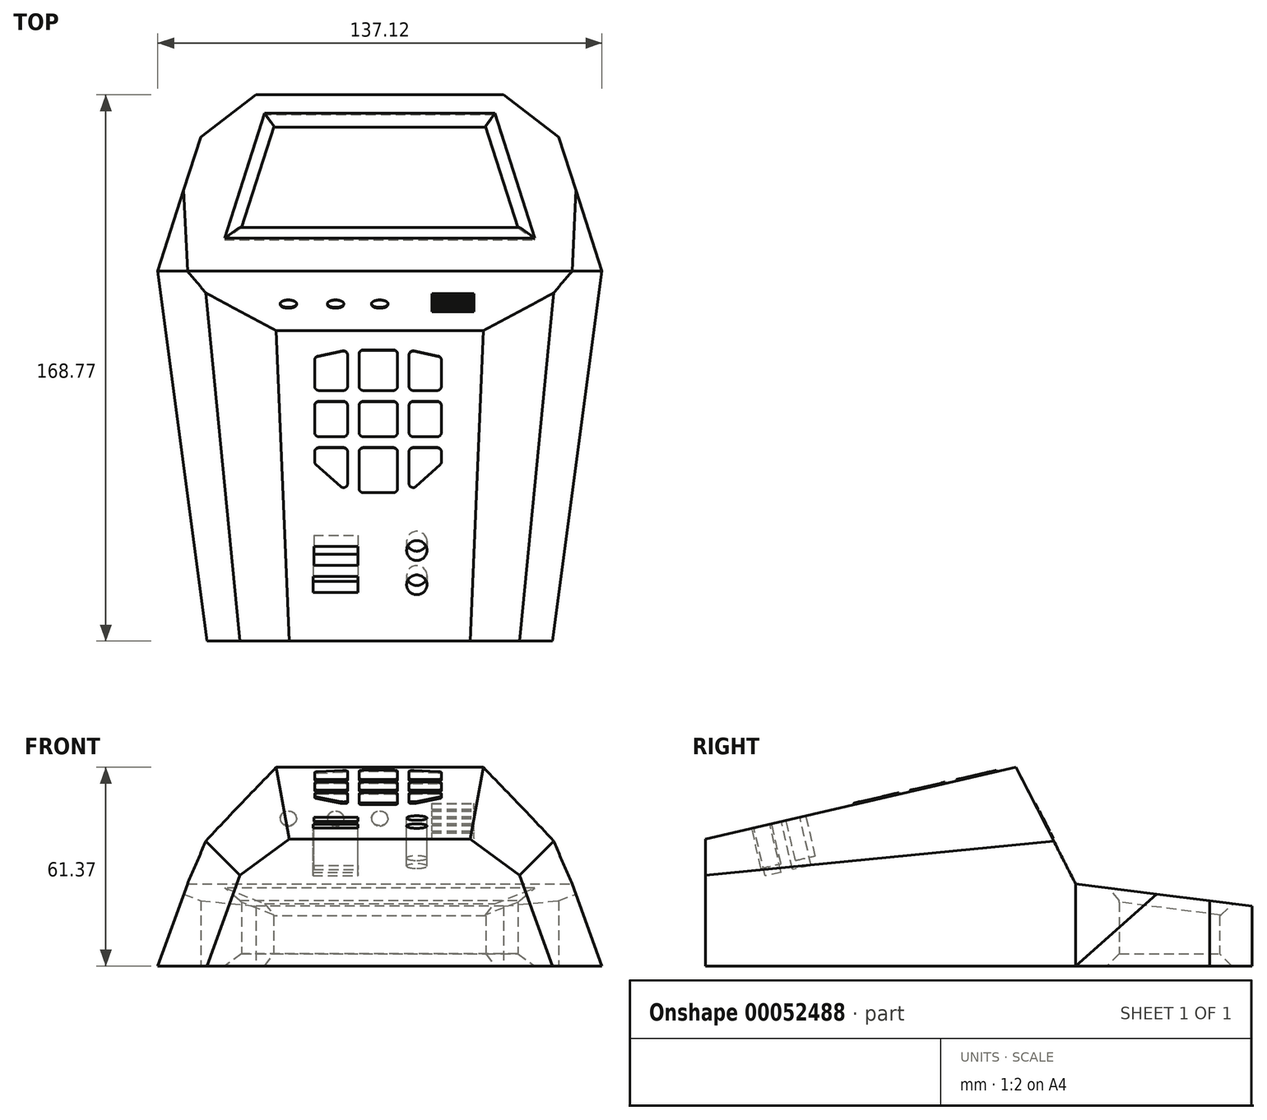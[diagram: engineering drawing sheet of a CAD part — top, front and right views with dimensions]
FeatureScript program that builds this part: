
annotation { "Feature Type Name" : "Feature", "Feature Type Description" : "" }
export const myFeature = defineFeature(function(context is Context, id is Id, definition is map)
    precondition{}
    {
        {
            var Q0;
            Q0=qCreatedBy(makeId("Front.planeOp"),FACE);
            var sketch = newSketch(context, id + "F0", { "sketchPlane" : qUnion([Q0])});
            skLineSegment(sketch, "E0", {"start": v(-27.94, 0) * mm, "end": v(27.94, 0) * mm});
            skLineSegment(sketch, "E1", {"start": v(27.94, 0) * mm, "end": v(43.18, -11.2) * mm});
            skLineSegment(sketch, "E2", {"start": v(43.18, -11.2) * mm, "end": v(53.34, -39.22) * mm});
            skLineSegment(sketch, "E3", {"start": v(53.34, -39.22) * mm, "end": v(-53.34, -39.22) * mm});
            skLineSegment(sketch, "E4", {"start": v(-53.34, -39.22) * mm, "end": v(-43.18, -11.2) * mm});
            skLineSegment(sketch, "E5", {"start": v(-43.18, -11.2) * mm, "end": v(-27.94, 0) * mm});
            skLineSegment(sketch, "E6", {"start": v(0, -39.22) * mm, "end": v(0, 0) * mm, "construction": true});
            skSolve(sketch);
        }
        {
            var Q0;
            Q0=qCreatedBy(makeId("Front.planeOp"),FACE);
            cPlane(context, id + "F1", {"entities" : qUnion([Q0]), "cplaneType" : CPlaneType.OFFSET, "offset" : 114.3 * mm, "oppositeDirection" : true, "width" : 152.4 * mm, "height" : 152.4 * mm});
        }
        {
            var Q0;
            Q0=qCreatedBy(id+"F1.planeOp",FACE);
            var sketch = newSketch(context, id + "F2", { "sketchPlane" : qUnion([Q0])});
            skLineSegment(sketch, "E7", {"start": v(-68.56, -39.22) * mm, "end": v(68.56, -39.22) * mm});
            skLineSegment(sketch, "E8", {"start": v(68.56, -39.22) * mm, "end": v(54.38, 0) * mm});
            skLineSegment(sketch, "E9", {"start": v(54.38, 0) * mm, "end": v(32.73, 26.38) * mm});
            skLineSegment(sketch, "E10", {"start": v(32.73, 26.38) * mm, "end": v(-32.73, 26.38) * mm});
            skLineSegment(sketch, "E11", {"start": v(-32.73, 26.38) * mm, "end": v(-54.38, 0) * mm});
            skLineSegment(sketch, "E12", {"start": v(-54.38, 0) * mm, "end": v(-68.56, -39.22) * mm});
            skLineSegment(sketch, "E13", {"start": v(0, -39.22) * mm, "end": v(0, 26.38) * mm, "construction": true});
            skSolve(sketch);
        }
        {
            var Q0;
            Q0=makeQuery(id+"F2.imprint","IMPRINT",FACE,{"disambiguationData":[TD([[makeQuery(id+"F2.imprint","IMPRINT",EDGE,{"derivedFrom":sQuery(id+"F2.wireOp",EDGE,"E7")}),1.0]])]});
            var Q1;
            Q1=makeQuery(id+"F0.imprint","IMPRINT",FACE,{"disambiguationData":[TD([[makeQuery(id+"F0.imprint","IMPRINT",EDGE,{"derivedFrom":sQuery(id+"F0.wireOp",EDGE,"E0")}),-1.0]])]});
            loft(context, id + "F3", {"sheetProfilesArray" : [{ "sheetProfileEntities" : qUnion([Q0]) }, { "sheetProfileEntities" : qUnion([Q1]) }]});
        }
        {
            var Q0;
            Q0=qCreatedBy(makeId("Right.planeOp"),FACE);
            var Q1;
            Q1=makeQuery(id+"F3.opLoft","MID_CAP_VERTEX",VERTEX,{"disambiguationData":[OSD([sQuery(id+"F2.wireOp",EDGE,"E7"),sQuery(id+"F2.wireOp",EDGE,"E12")])],"capPos":0.0});
            cPlane(context, id + "F4", {"entities" : qUnion([Q0, Q1]), "cplaneType" : CPlaneType.PLANE_POINT, "offset" : 152.4 * mm, "width" : 152.4 * mm, "height" : 152.4 * mm});
        }
        {
            var Q0;
            Q0=makeQuery(id+"F3.opLoft","SWEPT_FACE",FACE,{"disambiguationData":[OSD([sQuery(id+"F0.wireOp",EDGE,"E2"),sQuery(id+"F0.wireOp",EDGE,"E3"),sQuery(id+"F0.wireOp",EDGE,"E4"),sQuery(id+"F2.wireOp",EDGE,"E7"),sQuery(id+"F2.wireOp",EDGE,"E8"),sQuery(id+"F2.wireOp",EDGE,"E12")])]});
            var sketch = newSketch(context, id + "F5", { "sketchPlane" : qUnion([Q0])});
            skLineSegment(sketch, "E14", {"start": v(-68.56, -114.3) * mm, "end": v(-55.25, -155.74) * mm});
            skLineSegment(sketch, "E15", {"start": v(-55.25, -155.74) * mm, "end": v(-38.25, -168.77) * mm});
            skLineSegment(sketch, "E16", {"start": v(-38.25, -168.77) * mm, "end": v(38.25, -168.77) * mm});
            skLineSegment(sketch, "E17", {"start": v(38.25, -168.77) * mm, "end": v(55.25, -155.74) * mm});
            skLineSegment(sketch, "E18", {"start": v(55.25, -155.74) * mm, "end": v(68.56, -114.3) * mm});
            skLineSegment(sketch, "E19", {"start": v(-42.68, -127.84) * mm, "end": v(-32.74, -158.77) * mm});
            skLineSegment(sketch, "E20", {"start": v(-32.74, -158.77) * mm, "end": v(32.74, -158.77) * mm});
            skLineSegment(sketch, "E21", {"start": v(32.74, -158.77) * mm, "end": v(42.68, -127.84) * mm});
            skLineSegment(sketch, "E22", {"start": v(42.68, -127.84) * mm, "end": v(-42.68, -127.84) * mm});
            skLineSegment(sketch, "E23", {"start": v(0, -114.3) * mm, "end": v(0, -168.77) * mm, "construction": true});
            skPoint(sketch, "E23.endSnap0", {"position": v(0, -127.84) * mm});
            skSolve(sketch);
        }
        {
            var Q0;
            Q0=makeQuery(id+"F5.imprint","IMPRINT",FACE,{"disambiguationData":[TD([[makeQuery(id+"F5.imprint","IMPRINT",EDGE,{"derivedFrom":sQuery(id+"F5.wireOp",EDGE,"E14")}),1.0]])]});
            extrude(context, id + "F6", {"entities" : qUnion([Q0]), "operationType" : NewBodyOperationType.ADD, "oppositeDirection" : true, "depth" : 25.4 * mm});
        }
        {
            var Q0;
            Q0=qCreatedBy(id+"F4.planeOp",FACE);
            var sketch = newSketch(context, id + "F7", { "sketchPlane" : qUnion([Q0])});
            skLineSegment(sketch, "E24", {"start": v(114.3, -13.82) * mm, "end": v(95.96, 22.15) * mm});
            skLineSegment(sketch, "E25", {"start": v(95.96, 22.15) * mm, "end": v(114.3, 26.38) * mm});
            skLineSegment(sketch, "E26", {"start": v(114.3, 26.38) * mm, "end": v(114.3, -13.82) * mm});
            skSolve(sketch);
        }
        {
            var Q0;
            Q0 = qSketchRegion(id + "F7", true);
            extrude(context, id + "F8", {"entities" : qUnion([Q0]), "operationType" : NewBodyOperationType.REMOVE, "endBound" : BoundingType.THROUGH_ALL, "depth" : 25.4 * mm});
        }
        {
            var Q0;
            {var subQ0=sQuery(id+"F5.wireOp",EDGE,"E14");var subQ1=sQuery(id+"F2.wireOp",EDGE,"E8");var subQ2=sQuery(id+"F2.wireOp",EDGE,"E7");var subQ4=sQuery(id+"F2.wireOp",EDGE,"E12");Q0=makeQuery(id+"F6.boolean.opBoolean","SPLIT",FACE,{"disambiguationData":[TD([makeQuery(id+"F6.opExtrude","SWEPT_FACE",FACE,{"disambiguationData":[OSD([subQ0])]})])],"derivedFrom":makeQuery(id+"F6.opExtrude","SWEPT_FACE",FACE,{"disambiguationData":[OSD([subQ2,subQ1,subQ4])]})});}
            var sketch = newSketch(context, id + "F9", { "sketchPlane" : qUnion([Q0])});
            skLineSegment(sketch, "E27", {"start": v(-68.56, -39.22) * mm, "end": v(-59.38, -13.82) * mm});
            skLineSegment(sketch, "E28", {"start": v(-59.38, -13.82) * mm, "end": v(-68.56, -13.82) * mm});
            skLineSegment(sketch, "E29", {"start": v(-68.56, -13.82) * mm, "end": v(-68.56, -39.22) * mm});
            skLineSegment(sketch, "E30", {"start": v(68.56, -13.82) * mm, "end": v(59.38, -13.82) * mm});
            skLineSegment(sketch, "E31", {"start": v(59.38, -13.82) * mm, "end": v(68.56, -39.22) * mm});
            skLineSegment(sketch, "E32", {"start": v(68.56, -39.22) * mm, "end": v(68.56, -13.82) * mm});
            skSolve(sketch);
        }
        {
            var Q0;
            Q0 = qSketchRegion(id + "F9", true);
            extrude(context, id + "F10", {"entities" : qUnion([Q0]), "operationType" : NewBodyOperationType.REMOVE, "oppositeDirection" : true, "depth" : 25.4 * mm});
        }
        {
            var Q0;
            Q0=makeQuery(id+"F3.opLoft","SWEPT_FACE",FACE,{"disambiguationData":[OSD([sQuery(id+"F0.wireOp",EDGE,"E0"),sQuery(id+"F0.wireOp",EDGE,"E1"),sQuery(id+"F0.wireOp",EDGE,"E5"),sQuery(id+"F2.wireOp",EDGE,"E9"),sQuery(id+"F2.wireOp",EDGE,"E10"),sQuery(id+"F2.wireOp",EDGE,"E11")])]});
            var sketch = newSketch(context, id + "F11", { "sketchPlane" : qUnion([Q0])});
            skLineSegment(sketch, "E33", {"start": v(-19.08, 90.4) * mm, "end": v(-11.46, 92.02) * mm});
            skLineSegment(sketch, "E34", {"start": v(-9.93, 90.78) * mm, "end": v(-9.93, 80.86) * mm});
            skLineSegment(sketch, "E35", {"start": v(-11.2, 79.59) * mm, "end": v(-18.82, 79.59) * mm});
            skLineSegment(sketch, "E36", {"start": v(-20.09, 80.86) * mm, "end": v(-20.09, 89.17) * mm});
            skLineSegment(sketch, "E37", {"start": v(-5.1, 79.59) * mm, "end": v(4.2, 79.59) * mm});
            skLineSegment(sketch, "E38", {"start": v(5.47, 80.86) * mm, "end": v(5.47, 91.08) * mm});
            skLineSegment(sketch, "E39", {"start": v(4.2, 92.35) * mm, "end": v(-5.1, 92.35) * mm});
            skLineSegment(sketch, "E40", {"start": v(-6.37, 91.08) * mm, "end": v(-6.37, 80.86) * mm});
            skLineSegment(sketch, "E41", {"start": v(10.3, 79.59) * mm, "end": v(17.76, 79.59) * mm});
            skLineSegment(sketch, "E42", {"start": v(19.03, 80.86) * mm, "end": v(19.03, 89.17) * mm});
            skLineSegment(sketch, "E43", {"start": v(18.03, 90.41) * mm, "end": v(10.57, 92.02) * mm});
            skLineSegment(sketch, "E44", {"start": v(9.03, 90.78) * mm, "end": v(9.03, 80.86) * mm});
            skLineSegment(sketch, "E45", {"start": v(-20.09, 74.76) * mm, "end": v(-20.09, 66.2) * mm});
            skLineSegment(sketch, "E46", {"start": v(-18.82, 64.93) * mm, "end": v(-11.2, 64.93) * mm});
            skLineSegment(sketch, "E47", {"start": v(-9.93, 66.2) * mm, "end": v(-9.93, 74.76) * mm});
            skLineSegment(sketch, "E48", {"start": v(-11.2, 76.03) * mm, "end": v(-18.82, 76.03) * mm});
            skLineSegment(sketch, "E49", {"start": v(-6.37, 74.76) * mm, "end": v(-6.37, 66.2) * mm});
            skLineSegment(sketch, "E50", {"start": v(-5.1, 64.93) * mm, "end": v(4.2, 64.93) * mm});
            skLineSegment(sketch, "E51", {"start": v(5.47, 66.2) * mm, "end": v(5.47, 74.76) * mm});
            skLineSegment(sketch, "E52", {"start": v(4.2, 76.03) * mm, "end": v(-5.1, 76.03) * mm});
            skLineSegment(sketch, "E53", {"start": v(10.3, 76.03) * mm, "end": v(17.76, 76.03) * mm});
            skLineSegment(sketch, "E54", {"start": v(19.03, 74.76) * mm, "end": v(19.03, 66.2) * mm});
            skLineSegment(sketch, "E55", {"start": v(17.76, 64.93) * mm, "end": v(10.3, 64.93) * mm});
            skLineSegment(sketch, "E56", {"start": v(9.03, 66.2) * mm, "end": v(9.03, 74.76) * mm});
            skLineSegment(sketch, "E57", {"start": v(-20.09, 60.1) * mm, "end": v(-20.09, 56.95) * mm});
            skLineSegment(sketch, "E58", {"start": v(-19.67, 56) * mm, "end": v(-12.05, 49.1) * mm});
            skLineSegment(sketch, "E59", {"start": v(-9.93, 50.04) * mm, "end": v(-9.93, 60.1) * mm});
            skLineSegment(sketch, "E60", {"start": v(-11.2, 61.37) * mm, "end": v(-18.82, 61.37) * mm});
            skLineSegment(sketch, "E61", {"start": v(-6.37, 60.1) * mm, "end": v(-6.37, 48.44) * mm});
            skLineSegment(sketch, "E62", {"start": v(-5.1, 47.17) * mm, "end": v(4.2, 47.17) * mm});
            skLineSegment(sketch, "E63", {"start": v(5.47, 48.44) * mm, "end": v(5.47, 60.1) * mm});
            skLineSegment(sketch, "E64", {"start": v(4.2, 61.37) * mm, "end": v(-5.1, 61.37) * mm});
            skLineSegment(sketch, "E65", {"start": v(9.03, 60.1) * mm, "end": v(9.03, 50.07) * mm});
            skLineSegment(sketch, "E66", {"start": v(11.16, 49.14) * mm, "end": v(18.62, 56.01) * mm});
            skLineSegment(sketch, "E67", {"start": v(19.03, 56.94) * mm, "end": v(19.03, 60.1) * mm});
            skLineSegment(sketch, "E68", {"start": v(17.76, 61.37) * mm, "end": v(10.3, 61.37) * mm});
            skPoint(sketch, "E69.visualSharp", {"position": v(-20.09, 90.2) * mm});
            skArc(sketch, "E69.filletArc", {"start": v(-19.08, 90.4) * mm, "mid": v(-19.8, 89.96) * mm, "end": v(-20.09, 89.17) * mm});
            skPoint(sketch, "E70.visualSharp", {"position": v(-20.09, 79.59) * mm});
            skArc(sketch, "E70.filletArc", {"start": v(-20.09, 80.86) * mm, "mid": v(-19.72, 79.96) * mm, "end": v(-18.82, 79.59) * mm});
            skPoint(sketch, "E71.visualSharp", {"position": v(-9.93, 79.59) * mm});
            skArc(sketch, "E71.filletArc", {"start": v(-11.2, 79.59) * mm, "mid": v(-10.3, 79.96) * mm, "end": v(-9.93, 80.86) * mm});
            skPoint(sketch, "E72.visualSharp", {"position": v(-9.93, 92.35) * mm});
            skArc(sketch, "E72.filletArc", {"start": v(-9.93, 90.78) * mm, "mid": v(-10.4, 91.77) * mm, "end": v(-11.46, 92.02) * mm});
            skPoint(sketch, "E73.visualSharp", {"position": v(-6.37, 92.35) * mm});
            skArc(sketch, "E73.filletArc", {"start": v(-5.1, 92.35) * mm, "mid": v(-6, 91.98) * mm, "end": v(-6.37, 91.08) * mm});
            skPoint(sketch, "E74.visualSharp", {"position": v(-6.37, 79.59) * mm});
            skArc(sketch, "E74.filletArc", {"start": v(-6.37, 80.86) * mm, "mid": v(-6, 79.96) * mm, "end": v(-5.1, 79.59) * mm});
            skPoint(sketch, "E75.visualSharp", {"position": v(5.47, 92.35) * mm});
            skArc(sketch, "E75.filletArc", {"start": v(5.47, 91.08) * mm, "mid": v(5.1, 91.98) * mm, "end": v(4.2, 92.35) * mm});
            skPoint(sketch, "E76.visualSharp", {"position": v(5.47, 79.59) * mm});
            skArc(sketch, "E76.filletArc", {"start": v(4.2, 79.59) * mm, "mid": v(5.1, 79.96) * mm, "end": v(5.47, 80.86) * mm});
            skPoint(sketch, "E77.visualSharp", {"position": v(9.03, 92.35) * mm});
            skArc(sketch, "E77.filletArc", {"start": v(10.57, 92.02) * mm, "mid": v(9.5, 91.76) * mm, "end": v(9.03, 90.78) * mm});
            skPoint(sketch, "E78.visualSharp", {"position": v(9.03, 79.59) * mm});
            skArc(sketch, "E78.filletArc", {"start": v(9.03, 80.86) * mm, "mid": v(9.4, 79.96) * mm, "end": v(10.3, 79.59) * mm});
            skPoint(sketch, "E79.visualSharp", {"position": v(19.03, 90.2) * mm});
            skArc(sketch, "E79.filletArc", {"start": v(19.03, 89.17) * mm, "mid": v(18.75, 89.97) * mm, "end": v(18.03, 90.41) * mm});
            skPoint(sketch, "E80.visualSharp", {"position": v(19.03, 79.59) * mm});
            skArc(sketch, "E80.filletArc", {"start": v(17.76, 79.59) * mm, "mid": v(18.66, 79.96) * mm, "end": v(19.03, 80.86) * mm});
            skPoint(sketch, "E81.visualSharp", {"position": v(9.03, 76.03) * mm});
            skArc(sketch, "E81.filletArc", {"start": v(10.3, 76.03) * mm, "mid": v(9.4, 75.66) * mm, "end": v(9.03, 74.76) * mm});
            skPoint(sketch, "E82.visualSharp", {"position": v(19.03, 76.03) * mm});
            skArc(sketch, "E82.filletArc", {"start": v(19.03, 74.76) * mm, "mid": v(18.66, 75.66) * mm, "end": v(17.76, 76.03) * mm});
            skPoint(sketch, "E83.visualSharp", {"position": v(9.03, 64.93) * mm});
            skArc(sketch, "E83.filletArc", {"start": v(9.03, 66.2) * mm, "mid": v(9.4, 65.3) * mm, "end": v(10.3, 64.93) * mm});
            skPoint(sketch, "E84.visualSharp", {"position": v(19.03, 64.93) * mm});
            skArc(sketch, "E84.filletArc", {"start": v(17.76, 64.93) * mm, "mid": v(18.66, 65.3) * mm, "end": v(19.03, 66.2) * mm});
            skPoint(sketch, "E85.visualSharp", {"position": v(19.03, 61.37) * mm});
            skArc(sketch, "E85.filletArc", {"start": v(19.03, 60.1) * mm, "mid": v(18.66, 61) * mm, "end": v(17.76, 61.37) * mm});
            skPoint(sketch, "E86.visualSharp", {"position": v(9.03, 61.37) * mm});
            skArc(sketch, "E86.filletArc", {"start": v(10.3, 61.37) * mm, "mid": v(9.4, 61) * mm, "end": v(9.03, 60.1) * mm});
            skPoint(sketch, "E87.visualSharp", {"position": v(9.03, 47.17) * mm});
            skArc(sketch, "E87.filletArc", {"start": v(9.03, 50.07) * mm, "mid": v(9.79, 48.9) * mm, "end": v(11.16, 49.14) * mm});
            skPoint(sketch, "E88.visualSharp", {"position": v(19.03, 56.39) * mm});
            skArc(sketch, "E88.filletArc", {"start": v(18.62, 56.01) * mm, "mid": v(18.92, 56.43) * mm, "end": v(19.03, 56.94) * mm});
            skPoint(sketch, "E89.visualSharp", {"position": v(-6.37, 47.17) * mm});
            skArc(sketch, "E89.filletArc", {"start": v(-6.37, 48.44) * mm, "mid": v(-6, 47.55) * mm, "end": v(-5.1, 47.17) * mm});
            skPoint(sketch, "E90.visualSharp", {"position": v(5.47, 47.17) * mm});
            skArc(sketch, "E90.filletArc", {"start": v(4.2, 47.17) * mm, "mid": v(5.1, 47.55) * mm, "end": v(5.47, 48.44) * mm});
            skPoint(sketch, "E91.visualSharp", {"position": v(5.47, 61.37) * mm});
            skArc(sketch, "E91.filletArc", {"start": v(5.47, 60.1) * mm, "mid": v(5.1, 61) * mm, "end": v(4.2, 61.37) * mm});
            skPoint(sketch, "E92.visualSharp", {"position": v(-6.37, 61.37) * mm});
            skArc(sketch, "E92.filletArc", {"start": v(-5.1, 61.37) * mm, "mid": v(-6, 61) * mm, "end": v(-6.37, 60.1) * mm});
            skPoint(sketch, "E93.visualSharp", {"position": v(-6.37, 64.93) * mm});
            skArc(sketch, "E93.filletArc", {"start": v(-6.37, 66.2) * mm, "mid": v(-6, 65.3) * mm, "end": v(-5.1, 64.93) * mm});
            skPoint(sketch, "E94.visualSharp", {"position": v(5.47, 64.93) * mm});
            skArc(sketch, "E94.filletArc", {"start": v(4.2, 64.93) * mm, "mid": v(5.1, 65.3) * mm, "end": v(5.47, 66.2) * mm});
            skPoint(sketch, "E95.visualSharp", {"position": v(5.47, 76.03) * mm});
            skArc(sketch, "E95.filletArc", {"start": v(5.47, 74.76) * mm, "mid": v(5.1, 75.66) * mm, "end": v(4.2, 76.03) * mm});
            skPoint(sketch, "E96.visualSharp", {"position": v(-6.37, 76.03) * mm});
            skArc(sketch, "E96.filletArc", {"start": v(-5.1, 76.03) * mm, "mid": v(-6, 75.66) * mm, "end": v(-6.37, 74.76) * mm});
            skPoint(sketch, "E97.visualSharp", {"position": v(-9.93, 76.03) * mm});
            skArc(sketch, "E97.filletArc", {"start": v(-9.93, 74.76) * mm, "mid": v(-10.3, 75.66) * mm, "end": v(-11.2, 76.03) * mm});
            skPoint(sketch, "E98.visualSharp", {"position": v(-20.09, 76.03) * mm});
            skArc(sketch, "E98.filletArc", {"start": v(-18.82, 76.03) * mm, "mid": v(-19.72, 75.66) * mm, "end": v(-20.09, 74.76) * mm});
            skPoint(sketch, "E99.visualSharp", {"position": v(-20.09, 64.93) * mm});
            skArc(sketch, "E99.filletArc", {"start": v(-20.09, 66.2) * mm, "mid": v(-19.72, 65.3) * mm, "end": v(-18.82, 64.93) * mm});
            skPoint(sketch, "E100.visualSharp", {"position": v(-9.93, 64.93) * mm});
            skArc(sketch, "E100.filletArc", {"start": v(-11.2, 64.93) * mm, "mid": v(-10.3, 65.3) * mm, "end": v(-9.93, 66.2) * mm});
            skPoint(sketch, "E101.visualSharp", {"position": v(-20.09, 61.37) * mm});
            skArc(sketch, "E101.filletArc", {"start": v(-18.82, 61.37) * mm, "mid": v(-19.72, 61) * mm, "end": v(-20.09, 60.1) * mm});
            skPoint(sketch, "E102.visualSharp", {"position": v(-9.93, 61.37) * mm});
            skArc(sketch, "E102.filletArc", {"start": v(-9.93, 60.1) * mm, "mid": v(-10.3, 61) * mm, "end": v(-11.2, 61.37) * mm});
            skPoint(sketch, "E103.visualSharp", {"position": v(-9.93, 47.17) * mm});
            skArc(sketch, "E103.filletArc", {"start": v(-12.05, 49.1) * mm, "mid": v(-10.69, 48.88) * mm, "end": v(-9.93, 50.04) * mm});
            skPoint(sketch, "E104.visualSharp", {"position": v(-20.09, 56.39) * mm});
            skArc(sketch, "E104.filletArc", {"start": v(-20.09, 56.95) * mm, "mid": v(-19.98, 56.44) * mm, "end": v(-19.67, 56) * mm});
            skSolve(sketch);
        }
        {
            var Q0;
            Q0=makeQuery(id+"F11.imprint","IMPRINT",FACE,{"disambiguationData":[TD([[makeQuery(id+"F11.imprint","IMPRINT",EDGE,{"derivedFrom":sQuery(id+"F11.wireOp",EDGE,"E49")}),1.0]])]});
            var Q1;
            Q1 = qSketchRegion(id + "F11", true);
            extrude(context, id + "F12", {"entities" : qUnion([Q0, Q1]), "operationType" : NewBodyOperationType.ADD, "depth" : 0.5 * mm});
        }
        {
            var Q0;
            Q0=qCreatedBy(id+"F4.planeOp",FACE);
            var sketch = newSketch(context, id + "F13", { "sketchPlane" : qUnion([Q0])});
            skLineSegment(sketch, "E105", {"start": v(114.3, -13.82) * mm, "end": v(168.77, -20.72) * mm});
            skLineSegment(sketch, "E106", {"start": v(168.77, -20.72) * mm, "end": v(168.77, -13.82) * mm});
            skLineSegment(sketch, "E107", {"start": v(168.77, -13.82) * mm, "end": v(114.3, -13.82) * mm});
            skSolve(sketch);
        }
        {
            var Q0;
            Q0 = qSketchRegion(id + "F13", true);
            extrude(context, id + "F14", {"entities" : qUnion([Q0]), "operationType" : NewBodyOperationType.REMOVE, "endBound" : BoundingType.THROUGH_ALL, "depth" : 25.4 * mm});
        }
        {
            var Q0;
            Q0=makeQuery(id+"F6.opExtrude","CAP_EDGE",EDGE,{"disambiguationData":[OSD([sQuery(id+"F5.wireOp",EDGE,"E22")])],"isStart":false});
            var Q1;
            Q1=makeQuery(id+"F6.opExtrude","CAP_EDGE",EDGE,{"disambiguationData":[OSD([sQuery(id+"F5.wireOp",EDGE,"E19")])],"isStart":false});
            var Q2;
            Q2=makeQuery(id+"F6.opExtrude","CAP_EDGE",EDGE,{"disambiguationData":[OSD([sQuery(id+"F5.wireOp",EDGE,"E20")])],"isStart":false});
            var Q3;
            Q3=makeQuery(id+"F6.opExtrude","CAP_EDGE",EDGE,{"disambiguationData":[OSD([sQuery(id+"F5.wireOp",EDGE,"E21")])],"isStart":false});
            var Q4;
            Q4=makeQuery(id+"F6.opExtrude","CAP_EDGE",EDGE,{"disambiguationData":[OSD([sQuery(id+"F5.wireOp",EDGE,"E20")])],"isStart":true});
            var Q5;
            Q5=makeQuery(id+"F6.opExtrude","CAP_EDGE",EDGE,{"disambiguationData":[OSD([sQuery(id+"F5.wireOp",EDGE,"E19")])],"isStart":true});
            var Q6;
            Q6=makeQuery(id+"F6.opExtrude","CAP_EDGE",EDGE,{"disambiguationData":[OSD([sQuery(id+"F5.wireOp",EDGE,"E22")])],"isStart":true});
            var Q7;
            Q7=makeQuery(id+"F6.opExtrude","CAP_EDGE",EDGE,{"disambiguationData":[OSD([sQuery(id+"F5.wireOp",EDGE,"E21")])],"isStart":true});
            var Q8;
            Q8=makeQuery(id+"F14.boolean.opBoolean","INTERSECT",EDGE,{"derivedFrom":[makeQuery(id+"F6.opExtrude","SWEPT_FACE",FACE,{"disambiguationData":[OSD([sQuery(id+"F5.wireOp",EDGE,"E19")])]}),makeQuery(id+"F14.opExtrude","SWEPT_FACE",FACE,{"disambiguationData":[OSD([sQuery(id+"F13.wireOp",EDGE,"E105")])]})]});
            var Q9;
            Q9=makeQuery(id+"F14.boolean.opBoolean","INTERSECT",EDGE,{"derivedFrom":[makeQuery(id+"F6.opExtrude","SWEPT_FACE",FACE,{"disambiguationData":[OSD([sQuery(id+"F5.wireOp",EDGE,"E20")])]}),makeQuery(id+"F14.opExtrude","SWEPT_FACE",FACE,{"disambiguationData":[OSD([sQuery(id+"F13.wireOp",EDGE,"E105")])]})]});
            var Q10;
            Q10=makeQuery(id+"F14.boolean.opBoolean","INTERSECT",EDGE,{"derivedFrom":[makeQuery(id+"F6.opExtrude","SWEPT_FACE",FACE,{"disambiguationData":[OSD([sQuery(id+"F5.wireOp",EDGE,"E21")])]}),makeQuery(id+"F14.opExtrude","SWEPT_FACE",FACE,{"disambiguationData":[OSD([sQuery(id+"F13.wireOp",EDGE,"E105")])]})]});
            var Q11;
            Q11=makeQuery(id+"F14.boolean.opBoolean","INTERSECT",EDGE,{"derivedFrom":[makeQuery(id+"F6.opExtrude","SWEPT_FACE",FACE,{"disambiguationData":[OSD([sQuery(id+"F5.wireOp",EDGE,"E22")])]}),makeQuery(id+"F14.opExtrude","SWEPT_FACE",FACE,{"disambiguationData":[OSD([sQuery(id+"F13.wireOp",EDGE,"E105")])]})]});
            chamfer(context, id + "F15", {"entities" : qUnion([Q0, Q1, Q2, Q3, Q4, Q5, Q6, Q7, Q8, Q9, Q10, Q11]), "width" : 3.8 * mm, "tangentPropagation" : true});
        }
        {
            var Q0;
            Q0=makeQuery(id+"F3.opLoft","SWEPT_FACE",FACE,{"disambiguationData":[OSD([sQuery(id+"F0.wireOp",EDGE,"E0"),sQuery(id+"F0.wireOp",EDGE,"E1"),sQuery(id+"F0.wireOp",EDGE,"E5"),sQuery(id+"F2.wireOp",EDGE,"E9"),sQuery(id+"F2.wireOp",EDGE,"E10"),sQuery(id+"F2.wireOp",EDGE,"E11")])]});
            var sketch = newSketch(context, id + "F16", { "sketchPlane" : qUnion([Q0])});
            skLineSegment(sketch, "E108.bottom", {"start": v(-20.34, 29.96) * mm, "end": v(-6.7, 29.96) * mm});
            skLineSegment(sketch, "E108.top", {"start": v(-20.34, 24.08) * mm, "end": v(-6.7, 24.08) * mm});
            skLineSegment(sketch, "E108.left", {"start": v(-20.34, 29.96) * mm, "end": v(-20.34, 24.08) * mm});
            skLineSegment(sketch, "E108.right", {"start": v(-6.7, 29.96) * mm, "end": v(-6.7, 24.08) * mm});
            skLineSegment(sketch, "E109.bottom", {"start": v(-20.62, 20.44) * mm, "end": v(-6.7, 20.44) * mm});
            skLineSegment(sketch, "E109.top", {"start": v(-20.62, 15.4) * mm, "end": v(-6.7, 15.4) * mm});
            skLineSegment(sketch, "E109.left", {"start": v(-20.62, 20.44) * mm, "end": v(-20.62, 15.4) * mm});
            skLineSegment(sketch, "E109.right", {"start": v(-6.7, 20.44) * mm, "end": v(-6.7, 15.4) * mm});
            skSolve(sketch);
        }
        {
            var Q0;
            Q0 = qSketchRegion(id + "F16", true);
            extrude(context, id + "F17", {"entities" : qUnion([Q0]), "operationType" : NewBodyOperationType.REMOVE, "oppositeDirection" : true, "depth" : 15.24 * mm});
        }
        {
            var Q0;
            Q0=makeQuery(id+"F3.opLoft","SWEPT_FACE",FACE,{"disambiguationData":[OSD([sQuery(id+"F0.wireOp",EDGE,"E0"),sQuery(id+"F0.wireOp",EDGE,"E1"),sQuery(id+"F0.wireOp",EDGE,"E5"),sQuery(id+"F2.wireOp",EDGE,"E9"),sQuery(id+"F2.wireOp",EDGE,"E10"),sQuery(id+"F2.wireOp",EDGE,"E11")])]});
            var sketch = newSketch(context, id + "F18", { "sketchPlane" : qUnion([Q0])});
            skCircle(sketch, "E110", {"center": v(11.44, 28.73) * mm, "radius": 3.15 * mm});
            skCircle(sketch, "E111", {"center": v(11.44, 17.85) * mm, "radius": 3.15 * mm});
            skSolve(sketch);
        }
        {
            var Q0;
            Q0 = qSketchRegion(id + "F18", true);
            extrude(context, id + "F19", {"entities" : qUnion([Q0]), "operationType" : NewBodyOperationType.REMOVE, "oppositeDirection" : true, "depth" : 12.7 * mm});
        }
        {
            var Q0;
            Q0=makeQuery(id+"F8.boolean.opBoolean","COPY",FACE,{"derivedFrom":makeQuery(id+"F8.opExtrude","SWEPT_FACE",FACE,{"disambiguationData":[OSD([sQuery(id+"F7.wireOp",EDGE,"E24")])]})});
            var sketch = newSketch(context, id + "F20", { "sketchPlane" : qUnion([Q0])});
            skCircle(sketch, "E112", {"center": v(28.22, -41.66) * mm, "radius": 2.54 * mm});
            skCircle(sketch, "E113", {"center": v(13.64, -41.66) * mm, "radius": 2.54 * mm});
            skCircle(sketch, "E114", {"center": v(0, -41.66) * mm, "radius": 2.54 * mm});
            skLineSegment(sketch, "E115.bottom", {"start": v(-16.1, -48.6) * mm, "end": v(-29.12, -48.6) * mm});
            skLineSegment(sketch, "E115.top", {"start": v(-16.1, -46.66) * mm, "end": v(-29.12, -46.66) * mm});
            skLineSegment(sketch, "E115.left", {"start": v(-16.1, -48.6) * mm, "end": v(-16.1, -46.66) * mm});
            skLineSegment(sketch, "E115.right", {"start": v(-29.12, -48.6) * mm, "end": v(-29.12, -46.66) * mm});
            skLineSegment(sketch, "E116.bottom", {"start": v(-16.1, -46.06) * mm, "end": v(-29.12, -46.06) * mm});
            skLineSegment(sketch, "E116.top", {"start": v(-16.1, -44.12) * mm, "end": v(-29.12, -44.12) * mm});
            skLineSegment(sketch, "E116.left", {"start": v(-16.1, -46.06) * mm, "end": v(-16.1, -44.12) * mm});
            skLineSegment(sketch, "E116.right", {"start": v(-29.12, -46.06) * mm, "end": v(-29.12, -44.12) * mm});
            skLineSegment(sketch, "E117.bottom", {"start": v(-16.1, -43.52) * mm, "end": v(-29.12, -43.52) * mm});
            skLineSegment(sketch, "E117.top", {"start": v(-16.1, -41.59) * mm, "end": v(-29.12, -41.59) * mm});
            skLineSegment(sketch, "E117.left", {"start": v(-16.1, -43.52) * mm, "end": v(-16.1, -41.59) * mm});
            skLineSegment(sketch, "E117.right", {"start": v(-29.12, -43.52) * mm, "end": v(-29.12, -41.59) * mm});
            skLineSegment(sketch, "E118.bottom", {"start": v(-16.1, -40.99) * mm, "end": v(-29.12, -40.99) * mm});
            skLineSegment(sketch, "E118.top", {"start": v(-16.1, -39.05) * mm, "end": v(-29.12, -39.05) * mm});
            skLineSegment(sketch, "E118.left", {"start": v(-16.1, -40.99) * mm, "end": v(-16.1, -39.05) * mm});
            skLineSegment(sketch, "E118.right", {"start": v(-29.12, -40.99) * mm, "end": v(-29.12, -39.05) * mm});
            skLineSegment(sketch, "E119.bottom", {"start": v(-16.1, -38.45) * mm, "end": v(-29.12, -38.45) * mm});
            skLineSegment(sketch, "E119.top", {"start": v(-16.1, -36.52) * mm, "end": v(-29.12, -36.52) * mm});
            skLineSegment(sketch, "E119.left", {"start": v(-16.1, -38.45) * mm, "end": v(-16.1, -36.52) * mm});
            skLineSegment(sketch, "E119.right", {"start": v(-29.12, -38.45) * mm, "end": v(-29.12, -36.52) * mm});
            skLineSegment(sketch, "E120", {"start": v(-16.1, -46.66) * mm, "end": v(-16.1, -46.06) * mm, "construction": true});
            skLineSegment(sketch, "E121", {"start": v(-16.1, -44.12) * mm, "end": v(-16.1, -43.52) * mm, "construction": true});
            skLineSegment(sketch, "E122", {"start": v(-16.1, -41.59) * mm, "end": v(-16.1, -40.99) * mm, "construction": true});
            skLineSegment(sketch, "E123", {"start": v(-16.1, -39.05) * mm, "end": v(-16.1, -38.45) * mm, "construction": true});
            skSolve(sketch);
        }
        {
            var Q0;
            Q0 = qSketchRegion(id + "F20", true);
            extrude(context, id + "F21", {"entities" : qUnion([Q0]), "operationType" : NewBodyOperationType.ADD, "depth" : 0.25 * mm});
        }
    });
